FCSTD DOCUMENT  (FreeCAD 1.0RUnknown)
Label: wardrobe_drawer_jan
License: All rights reserved
objects: App::FeaturePython×11, App::Link×7, Assembly::JointGroup×1, Assembly::AssemblyObject×1
EXTERNAL_REF file=../purchased parts/hettich_rail_550mm.FCStd obj=Body
EXTERNAL_REF file=parts/drawer_sides.FCStd obj=Body
EXTERNAL_REF file=parts/drawer_back.FCStd obj=Body
EXTERNAL_REF file=parts/drawer_bottom.FCStd obj=Body
EXTERNAL_REF file=parts/drawer_front.FCStd obj=Body

FEATURE [App::Link] hettich_rail_550
  LinkPlacement = pos=(0,-8.67788e-07,0) rot=(0.57735,0.57735,0.57735;2.0944rad)
  LinkedObject = -> <external ../purchased parts/hettich_rail_550mm.FCStd>#Body
  Placement = pos=(0,-8.67788e-07,0) rot=(0.57735,0.57735,0.57735;2.0944rad)
FEATURE [App::Link] hettich_rail_551  label="hettich_rail_550_1"
  LinkPlacement = pos=(502,3.32992e-05,-3.4167e-05) rot=(0.57735,-0.57735,-0.57735;2.0944rad)
  LinkedObject = -> <external ../purchased parts/hettich_rail_550mm.FCStd>#Body
  Placement = pos=(502,3.32992e-05,-3.4167e-05) rot=(0.57735,-0.57735,-0.57735;2.0944rad)
FEATURE [App::Link] drawer_sides
  LinkPlacement = pos=(22,256,72.5) rot=(-0.340731,0.659269,0.659269;0rad)
  LinkedObject = -> <external parts/drawer_sides.FCStd>#Body
  Placement = pos=(22,256,72.5) rot=(-0.340731,0.659269,0.659269;0rad)
FEATURE [App::Link] drawer_sides001
  LinkPlacement = pos=(480,-256,72.5) rot=(0,0,1;3.14159rad)
  LinkedObject = -> <external parts/drawer_sides.FCStd>#Body
  Placement = pos=(480,-256,72.5) rot=(0,0,1;3.14159rad)
FEATURE [App::Link] drawer_back
  LinkPlacement = pos=(489.5,265.5,80.75) rot=(0,0,-1;1.5708rad)
  LinkedObject = -> <external parts/drawer_back.FCStd>#Body
  Placement = pos=(489.5,265.5,80.75) rot=(0,0,-1;1.5708rad)
FEATURE [App::Link] drawer_bottom
  LinkPlacement = pos=(251,5.75002,-2.50002) rot=(0,0,1;3.14159rad)
  LinkedObject = -> <external parts/drawer_bottom.FCStd>#Body
  Placement = pos=(251,5.75002,-2.50002) rot=(0,0,1;3.14159rad)
FEATURE [App::Link] drawer_front
  LinkPlacement = pos=(12.5,-265.5,72.5) rot=(0,0,1;1.5708rad)
  LinkedObject = -> <external parts/drawer_front.FCStd>#Body
  Placement = pos=(12.5,-265.5,72.5) rot=(0,0,1;1.5708rad)
FEATURE [App::FeaturePython] GroundedJoint  # Assembly grounded joint (typed FeaturePython)
  ObjectToGround = -> hettich_rail_550
  Placement = pos=(0,-8.67788e-07,0) rot=(0.57735,0.57735,0.57735;2.0944rad)
FEATURE [App::FeaturePython] Joint  label="Gleitverbindung"  # Assembly joint (typed FeaturePython)
  Activated = true
  AngleMax = 0
  AngleMin = 0
  Detach1 = false
  Detach2 = false
  Distance = 0
  Distance2 = 0
  EnableAngleMax = false
  EnableAngleMin = false
  EnableLengthMax = true
  EnableLengthMin = true
  JointType = 3 (Slider)
  LengthMax = 275
  LengthMin = -100
  Offset2 = pos=(0,0,0) rot=(0,0,1;1.5708rad)
  Placement1 = pos=(-9.5,-256,-85) rot=(-0.57735,-0.57735,0.57735;4.18879rad)
  Placement2 = pos=(-275,-12.5,12.5) rot=(-0.57735,0.57735,0.57735;4.18879rad)
  Reference1 = -> Assembly [drawer_sides.Edge8,drawer_sides.Edge8]
  Reference2 = -> Assembly [hettich_rail_550.Edge16,hettich_rail_550.Vertex11]
FEATURE [App::FeaturePython] Joint003  label="Parallel"  # Assembly joint (typed FeaturePython)
  Activated = true
  AngleMax = 0
  AngleMin = 0
  Detach1 = false
  Detach2 = false
  Distance = 0
  Distance2 = 0
  EnableAngleMax = false
  EnableAngleMin = false
  EnableLengthMax = false
  EnableLengthMin = false
  JointType = 6 (Parallel)
  LengthMax = 0
  LengthMin = 0
  Placement1 = pos=(275,-12.5,12.5) rot=(0,0,1;0rad)
  Placement2 = pos=(-4e-16,2.5,12.5) rot=(0,0,1;0rad)
  Reference1 = -> Assembly [hettich_rail_550.Face5,hettich_rail_550.Vertex12]
  Reference2 = -> Assembly [hettich_rail_551.Face5,hettich_rail_551.Face5]
FEATURE [App::FeaturePython] Joint004  label="Parallel001"  # Assembly joint (typed FeaturePython)
  Activated = true
  AngleMax = 0
  AngleMin = 0
  Detach1 = false
  Detach2 = false
  Distance = 0
  Distance2 = 0
  EnableAngleMax = false
  EnableAngleMin = false
  EnableLengthMax = false
  EnableLengthMin = false
  JointType = 6 (Parallel)
  LengthMax = 0
  LengthMin = 0
  Placement1 = pos=(275,-12.5,25.5) rot=(0,-0.707107,0.707107;3.14159rad)
  Placement2 = pos=(-275,-12.5,25.5) rot=(0,0.707107,-0.707107;3.14159rad)
  Reference1 = -> Assembly [hettich_rail_550.Face7,hettich_rail_550.Vertex15]
  Reference2 = -> Assembly [hettich_rail_551.Face7,hettich_rail_551.Vertex16]
FEATURE [App::FeaturePython] Joint005  label="Parallel002"  # Assembly joint (typed FeaturePython)
  Activated = true
  AngleMax = 0
  AngleMin = 0
  Detach1 = false
  Detach2 = false
  Distance = 0
  Distance2 = 0
  EnableAngleMax = false
  EnableAngleMin = false
  EnableLengthMax = false
  EnableLengthMin = false
  JointType = 6 (Parallel)
  LengthMax = 0
  LengthMin = 0
  Placement1 = pos=(275,-0.565372,6.79404) rot=(-0.707107,0,-0.707107;3.14159rad)
  Placement2 = pos=(-275,-0.565372,6.79404) rot=(-0.707107,0,0.707107;3.14159rad)
  Reference1 = -> Assembly [hettich_rail_550.Face10,hettich_rail_550.Face10]
  Reference2 = -> Assembly [hettich_rail_551.Face9,hettich_rail_551.Face9]
FEATURE [App::FeaturePython] Joint006  label="Abstand"  # Assembly joint (typed FeaturePython)
  Activated = true
  AngleMax = 0
  AngleMin = 0
  Detach1 = false
  Detach2 = false
  Distance = 0
  Distance2 = 0
  EnableAngleMax = false
  EnableAngleMin = false
  EnableLengthMax = false
  EnableLengthMin = false
  JointType = 5 (Distance)
  LengthMax = 0
  LengthMin = 0
  Placement1 = pos=(275,-0.565372,6.79404) rot=(-0.707107,0,-0.707107;3.14159rad)
  Placement2 = pos=(-275,-0.565372,6.79404) rot=(-0.707107,0,0.707107;3.14159rad)
  Reference1 = -> Assembly [hettich_rail_550.Face10,hettich_rail_550.Face10]
  Reference2 = -> Assembly [hettich_rail_551.Face9,hettich_rail_551.Face9]
FEATURE [App::FeaturePython] Joint007  label="StarrerVerbund"  # Assembly joint (typed FeaturePython)
  Activated = true
  AngleMax = 0
  AngleMin = 0
  Detach1 = false
  Detach2 = false
  Distance = 0
  Distance2 = 0
  EnableAngleMax = false
  EnableAngleMin = false
  EnableLengthMax = false
  EnableLengthMin = false
  JointType = 0 (Fixed)
  LengthMax = 0
  LengthMin = 0
  Offset2 = pos=(0,0,0) rot=(0,0,1;1.5708rad)
  Placement1 = pos=(9.5,1.8e-15,85) rot=(0,0,1;0rad)
  Placement2 = pos=(-9.5,-512,85) rot=(0.707107,0.707107,0;3.14159rad)
  Reference1 = -> Assembly [drawer_front.Edge3,drawer_front.Vertex3]
  Reference2 = -> Assembly [drawer_sides.Edge10,drawer_sides.Vertex6]
FEATURE [App::FeaturePython] Joint009  label="Gleitverbindung001"  # Assembly joint (typed FeaturePython)
  Activated = true
  AngleMax = 0
  AngleMin = 0
  Detach1 = false
  Detach2 = false
  Distance = 0
  Distance2 = 0
  EnableAngleMax = false
  EnableAngleMin = false
  EnableLengthMax = false
  EnableLengthMin = false
  JointType = 3 (Slider)
  LengthMax = 0
  LengthMin = 0
  Placement1 = pos=(275,-12.5,12.5) rot=(-0.707107,0,0.707107;3.14159rad)
  Placement2 = pos=(-9.5,-256,-85) rot=(-0.57735,-0.57735,0.57735;4.18879rad)
  Reference1 = -> Assembly [hettich_rail_551.Edge16,hettich_rail_551.Vertex12]
  Reference2 = -> Assembly [drawer_sides001.Edge8,drawer_sides001.Edge8]
FEATURE [App::FeaturePython] Joint010  label="StarrerVerbund002"  # Assembly joint (typed FeaturePython)
  Activated = true
  AngleMax = 0
  AngleMin = 0
  Detach1 = false
  Detach2 = false
  Distance = 0
  Distance2 = 0
  EnableAngleMax = false
  EnableAngleMin = false
  EnableLengthMax = false
  EnableLengthMin = false
  JointType = 0 (Fixed)
  LengthMax = 0
  LengthMin = 0
  Offset2 = pos=(0,0,0) rot=(0,0,-1;1.5708rad)
  Placement1 = pos=(9.5,-477,76.75) rot=(0,0,1;0rad)
  Placement2 = pos=(-9.5,-5.68e-14,85) rot=(-0.707107,0.707107,0;3.14159rad)
  Reference1 = -> Assembly [drawer_back.Edge7,drawer_back.Vertex6]
  Reference2 = -> Assembly [drawer_sides.Edge9,drawer_sides.Vertex5]
FEATURE [App::FeaturePython] Joint011  label="StarrerVerbund003"  # Assembly joint (typed FeaturePython)
  Activated = true
  AngleMax = 0
  AngleMin = 0
  Detach1 = false
  Detach2 = false
  Distance = 0
  Distance2 = 0
  EnableAngleMax = false
  EnableAngleMin = false
  EnableLengthMax = false
  EnableLengthMin = false
  JointType = 0 (Fixed)
  LengthMax = 0
  LengthMin = 0
  Placement1 = pos=(-9.5,0,85) rot=(0,1,0;3.14159rad)
  Placement2 = pos=(9.5,-477,85) rot=(0,0,1;0rad)
  Reference1 = -> Assembly [drawer_sides001.Edge9,drawer_sides001.Vertex5]
  Reference2 = -> Assembly [drawer_front.Edge4,drawer_front.Vertex4]
FEATURE [App::FeaturePython] Joint012  label="StarrerVerbund004"  # Assembly joint (typed FeaturePython)
  Activated = true
  AngleMax = 0
  AngleMin = 0
  Detach1 = false
  Detach2 = false
  Distance = 0
  Distance2 = 0
  EnableAngleMax = false
  EnableAngleMin = false
  EnableLengthMax = false
  EnableLengthMin = false
  JointType = 0 (Fixed)
  LengthMax = 0
  LengthMin = 0
  Placement1 = pos=(0,269.75,0) rot=(-0.707107,0,0.707107;3.14159rad)
  Placement2 = pos=(1.5,-238.5,-75) rot=(-0.57735,-0.57735,0.57735;4.18879rad)
  Reference1 = -> Assembly [drawer_bottom.Edge9,drawer_bottom.Edge9]
  Reference2 = -> Assembly [drawer_front.Edge17,drawer_front.Edge17]
FEATURE [Assembly::JointGroup] Joints
  Group = -> [GroundedJoint,Joint,Joint003,Joint004,Joint005,Joint006,Joint007,Joint009,Joint010,Joint011,Joint012]
FEATURE [Assembly::AssemblyObject] Assembly  label="wardrobe_drawer_jan"
  Group = -> [Joints,hettich_rail_550,hettich_rail_551,drawer_sides,drawer_sides001,drawer_back,drawer_bottom,drawer_front,GroundedJoint,Joint,Joint003,Joint004,Joint005,Joint006,Joint007,Joint009,Joint010,Joint011,Joint012]
  Origin = -> Origin
  Type = Assembly

RESOLVED EXTERNAL PARTS (link-assembly join: the EXTERNAL_REF files above that resolve inside this repo's crawl, each included once):
---- part parts/drawer_back.FCStd = doc fcstd_10e94b67beff ----
FCSTD DOCUMENT  (FreeCAD 1.0RUnknown)
Label: drawer_back
License: All rights reserved
objects: PartDesign::CoordinateSystem×2, Sketcher::SketchObject×1, PartDesign::Pad×1, PartDesign::Body×1
note: 8 computed .brp shape members not serialized (recipe doc carries the construction recipe); baked Part::Feature solids carry a one-line shape summary decoded from their .brp
EXTERNAL_REF file=../../mastersketch.FCStd obj=Spreadsheet

FEATURE [Sketcher::SketchObject] Sketch
  ArcFitTolerance = 1e-06
  AttachmentSupport = -> [XZ_Plane]
  FullyConstrained = true
  MakeInternals = false
  MapMode = 5
  Placement = pos=(0,0,0) rot=(1,0,0;1.5708rad)
  expr: Constraints[10] = mastersketch#Spreadsheet.drawer_outer_thickness
  expr: Constraints[11] = mastersketch#Spreadsheet.drawer_height - (mastersketch#Spreadsheet.drawer_bottom_thickness + mastersketch#Spreadsheet.drawer_bottom_tol + mastersketch#Spreadsheet.drawer_slot_height)
  sketch-geometry (5):
    g0: LineSegment StartX=-9.5 StartY=-76.75 StartZ=0 EndX=9.5 EndY=-76.75 EndZ=0
    g1: LineSegment StartX=9.5 StartY=-76.75 StartZ=0 EndX=9.5 EndY=76.75 EndZ=0
    g2: LineSegment StartX=9.5 StartY=76.75 StartZ=0 EndX=-9.5 EndY=76.75 EndZ=0
    g3: LineSegment StartX=-9.5 StartY=76.75 StartZ=0 EndX=-9.5 EndY=-76.75 EndZ=0
    g4: GeomPoint [constr] X=0 Y=0 Z=0
  constraints (12):
    c: Coincident(g0,g1)
    c: Coincident(g1,g2)
    c: Coincident(g2,g3)
    c: Coincident(g3,g0)
    c: Horizontal(g0)
    c: Horizontal(g2)
    c: Vertical(g1)
    c: Vertical(g3)
    c: Symmetric(g2,g0,g4)
    c: Coincident(g4,g-1)
    c: DistanceX(g0,g0) = 19
    c: DistanceY(g1,g1) = 153.5
FEATURE [PartDesign::Pad] Pad
  Direction = (0,-1,2e-16)
  Length = 477
  Length2 = 10
  Placement = pos=(0,0,0) rot=(1,0,0;1.5708rad)
  Profile = -> Sketch
  ReferenceAxis = -> Sketch [N_Axis]
  Refine = true
  Suppressed = false
  Type = 0
  expr: Length = mastersketch#Spreadsheet.drawer_width
FEATURE [PartDesign::CoordinateSystem] LCS_left
  AttacherType = Attacher::AttachEngine3D
  AttachmentSupport = -> [Pad]
  MapMode = 7
  Placement = pos=(9.5,-477,76.75) rot=(0,1,0;3.14159rad)
FEATURE [PartDesign::CoordinateSystem] LCS_right
  AttacherType = Attacher::AttachEngine3D
  AttachmentSupport = -> [Pad]
  MapMode = 7
  Placement = pos=(9.5,0,76.75) rot=(0,1,0;3.14159rad)
FEATURE [PartDesign::Body] Body  label="drawer_back"
  AllowCompound = false
  Group = -> [Sketch,Pad,LCS_left,LCS_right]
  Origin = -> Origin
  Tip = -> Pad
---- part parts/drawer_bottom.FCStd = doc fcstd_674dae41beb6 ----
FCSTD DOCUMENT  (FreeCAD 1.0RUnknown)
Label: drawer_bottom
License: All rights reserved
objects: Sketcher::SketchObject×1, PartDesign::Pad×1, PartDesign::CoordinateSystem×1, PartDesign::Body×1
note: 7 computed .brp shape members not serialized (recipe doc carries the construction recipe); baked Part::Feature solids carry a one-line shape summary decoded from their .brp
EXTERNAL_REF file=../../mastersketch.FCStd obj=Spreadsheet

FEATURE [Sketcher::SketchObject] Sketch
  ArcFitTolerance = 1e-06
  AttachmentSupport = -> [XY_Plane]
  FullyConstrained = true
  MakeInternals = false
  MapMode = 5
  expr: Constraints[10] = mastersketch#Spreadsheet.drawer_width + 2 * (mastersketch#Spreadsheet.drawer_slot_depth + mastersketch#Spreadsheet.drawer_bottom_tol) - 2 * mastersketch#Spreadsheet.drawer_outer_thickness - 2
  expr: Constraints[11] = mastersketch#Spreadsheet.drawer_length + mastersketch#Spreadsheet.drawer_slot_depth + mastersketch#Spreadsheet.drawer_bottom_tol - mastersketch#Spreadsheet.drawer_outer_thickness
  sketch-geometry (5):
    g0: LineSegment StartX=-227 StartY=-269.75 StartZ=0 EndX=227 EndY=-269.75 EndZ=0
    g1: LineSegment StartX=227 StartY=-269.75 StartZ=0 EndX=227 EndY=269.75 EndZ=0
    g2: LineSegment StartX=227 StartY=269.75 StartZ=0 EndX=-227 EndY=269.75 EndZ=0
    g3: LineSegment StartX=-227 StartY=269.75 StartZ=0 EndX=-227 EndY=-269.75 EndZ=0
    g4: GeomPoint [constr] X=0 Y=0 Z=0
  constraints (12):
    c: Coincident(g0,g1)
    c: Coincident(g1,g2)
    c: Coincident(g2,g3)
    c: Coincident(g3,g0)
    c: Horizontal(g0)
    c: Horizontal(g2)
    c: Vertical(g1)
    c: Vertical(g3)
    c: Symmetric(g2,g0,g4)
    c: Coincident(g4,g-1)
    c: DistanceX(g0,g0) = 454
    c: DistanceY(g1,g1) = 539.5
FEATURE [PartDesign::Pad] Pad
  Direction = (0,0,1)
  Length = 6
  Length2 = 10
  Profile = -> Sketch
  ReferenceAxis = -> Sketch [N_Axis]
  Refine = true
  Suppressed = false
  Type = 0
  expr: Length = mastersketch#Spreadsheet.drawer_bottom_thickness
FEATURE [PartDesign::CoordinateSystem] LCS_front
  AttacherType = Attacher::AttachEngine3D
  AttachmentSupport = -> [Pad]
  MapMode = 45
  Placement = pos=(0,-269.75,0) rot=(0.57735,0.57735,0.57735;2.0944rad)
FEATURE [PartDesign::Body] Body  label="drawer_bottom"
  AllowCompound = false
  Group = -> [Sketch,Pad,LCS_front]
  Origin = -> Origin
  Tip = -> Pad
---- part parts/drawer_front.FCStd = doc fcstd_8f72376a405c ----
FCSTD DOCUMENT  (FreeCAD 1.0RUnknown)
Label: drawer_front
License: All rights reserved
objects: PartDesign::CoordinateSystem×3, Sketcher::SketchObject×1, PartDesign::Pad×1, PartDesign::Body×1
note: 9 computed .brp shape members not serialized (recipe doc carries the construction recipe); baked Part::Feature solids carry a one-line shape summary decoded from their .brp
EXTERNAL_REF file=../../mastersketch.FCStd obj=Spreadsheet

FEATURE [Sketcher::SketchObject] Sketch
  ArcFitTolerance = 1e-06
  AttachmentSupport = -> [XZ_Plane]
  FullyConstrained = true
  MakeInternals = false
  MapMode = 5
  Placement = pos=(0,0,0) rot=(1,0,0;1.5708rad)
  expr: Constraints[13] = mastersketch#Spreadsheet.drawer_outer_thickness
  expr: Constraints[19] = mastersketch#Spreadsheet.drawer_bottom_thickness + mastersketch#Spreadsheet.drawer_bottom_tol
  expr: Constraints[20] = mastersketch#Spreadsheet.drawer_slot_height
  expr: Constraints[21] = mastersketch#Spreadsheet.drawer_height
  expr: Constraints[22] = mastersketch#Spreadsheet.drawer_slot_depth
  sketch-geometry (9):
    g0: LineSegment StartX=-9.5 StartY=-85 StartZ=0 EndX=9.5 EndY=-85 EndZ=0
    g1: LineSegment StartX=9.5 StartY=-85 StartZ=0 EndX=9.5 EndY=-75 EndZ=0
    g2: LineSegment StartX=9.5 StartY=85 StartZ=0 EndX=-9.5 EndY=85 EndZ=0
    g3: LineSegment StartX=-9.5 StartY=85 StartZ=0 EndX=-9.5 EndY=-85 EndZ=0
    g4: GeomPoint [constr] X=0 Y=0 Z=0
    g5: LineSegment StartX=9.5 StartY=-68.5 StartZ=0 EndX=1.5 EndY=-68.5 EndZ=0
    g6: LineSegment StartX=1.5 StartY=-68.5 StartZ=0 EndX=1.5 EndY=-75 EndZ=0
    g7: LineSegment StartX=1.5 StartY=-75 StartZ=0 EndX=9.5 EndY=-75 EndZ=0
    g8: LineSegment StartX=9.5 StartY=-68.5 StartZ=0 EndX=9.5 EndY=85 EndZ=0
  constraints (23):
    c: Coincident(g0,g1)
    c: Coincident(g8,g2)
    c: Coincident(g2,g3)
    c: Coincident(g3,g0)
    c: Horizontal(g0)
    c: Vertical(g1)
    c: Symmetric(g2,g0,g4)
    c: Coincident(g4,g-1)
    c: Coincident(g5,g6)
    c: Coincident(g6,g7)
    c: Vertical(g6)
    c: Horizontal(g5)
    c: Horizontal(g7)
    c: DistanceX(g2,g2) = 19
    c: Parallel(g3,g8)
    c: Coincident(g5,g8)
    c: Coincident(g7,g1)
    c: Vertical(g5,g1)
    c: Symmetric(g2,g2,g-2)
    c: Distance(g5,g1) = 6.5
    c: Distance(g6,g0) = 10
    c: DistanceY(g3,g3) = 170
    c: DistanceX(g5,g5) = 8
FEATURE [PartDesign::Pad] Pad
  Direction = (0,-1,2e-16)
  Length = 477
  Length2 = 10
  Placement = pos=(0,0,0) rot=(1,0,0;1.5708rad)
  Profile = -> Sketch
  ReferenceAxis = -> Sketch [N_Axis]
  Refine = true
  Suppressed = false
  Type = 0
  expr: Length = mastersketch#Spreadsheet.drawer_width
FEATURE [PartDesign::CoordinateSystem] LCS_left
  AttacherType = Attacher::AttachEngine3D
  AttachmentSupport = -> [Pad]
  MapMode = 7
  Placement = pos=(9.5,0,85) rot=(0,1,0;3.14159rad)
FEATURE [PartDesign::CoordinateSystem] LCS_right
  AttacherType = Attacher::AttachEngine3D
  AttachmentSupport = -> [Pad]
  MapMode = 7
  Placement = pos=(9.5,-477,85) rot=(0,1,0;3.14159rad)
FEATURE [PartDesign::CoordinateSystem] LCS_bottom_center
  AttacherType = Attacher::AttachEngine3D
  AttachmentSupport = -> [Pad]
  MapMode = 45
  Placement = pos=(1.5,-238.5,-75) rot=(0,0.707107,0.707107;3.14159rad)
FEATURE [PartDesign::Body] Body  label="drawer_front"
  AllowCompound = false
  Group = -> [Sketch,Pad,LCS_left,LCS_right,LCS_bottom_center]
  Origin = -> Origin
  Tip = -> Pad
---- part parts/drawer_sides.FCStd = doc fcstd_b4c7660c6d1a ----
FCSTD DOCUMENT  (FreeCAD 1.0RUnknown)
Label: drawer_sides
License: All rights reserved
objects: PartDesign::CoordinateSystem×3, Sketcher::SketchObject×1, PartDesign::Pad×1, PartDesign::Body×1
note: 9 computed .brp shape members not serialized (recipe doc carries the construction recipe); baked Part::Feature solids carry a one-line shape summary decoded from their .brp
EXTERNAL_REF file=../../mastersketch.FCStd obj=Spreadsheet

FEATURE [Sketcher::SketchObject] Sketch
  ArcFitTolerance = 1e-06
  AttachmentSupport = -> [XZ_Plane]
  FullyConstrained = true
  MakeInternals = false
  MapMode = 5
  Placement = pos=(0,0,0) rot=(1,0,0;1.5708rad)
  expr: Constraints[13] = mastersketch#Spreadsheet.drawer_outer_thickness
  expr: Constraints[19] = mastersketch#Spreadsheet.drawer_bottom_thickness + mastersketch#Spreadsheet.drawer_bottom_tol
  expr: Constraints[20] = mastersketch#Spreadsheet.drawer_slot_height
  expr: Constraints[21] = mastersketch#Spreadsheet.drawer_height
  expr: Constraints[22] = mastersketch#Spreadsheet.drawer_slot_depth
  sketch-geometry (9):
    g0: LineSegment StartX=-9.5 StartY=-85 StartZ=0 EndX=9.5 EndY=-85 EndZ=0
    g1: LineSegment StartX=9.5 StartY=-85 StartZ=0 EndX=9.5 EndY=-75 EndZ=0
    g2: LineSegment StartX=9.5 StartY=85 StartZ=0 EndX=-9.5 EndY=85 EndZ=0
    g3: LineSegment StartX=-9.5 StartY=85 StartZ=0 EndX=-9.5 EndY=-85 EndZ=0
    g4: GeomPoint [constr] X=0 Y=0 Z=0
    g5: LineSegment StartX=9.5 StartY=-68.5 StartZ=0 EndX=1.5 EndY=-68.5 EndZ=0
    g6: LineSegment StartX=1.5 StartY=-68.5 StartZ=0 EndX=1.5 EndY=-75 EndZ=0
    g7: LineSegment StartX=1.5 StartY=-75 StartZ=0 EndX=9.5 EndY=-75 EndZ=0
    g8: LineSegment StartX=9.5 StartY=-68.5 StartZ=0 EndX=9.5 EndY=85 EndZ=0
  constraints (23):
    c: Coincident(g0,g1)
    c: Coincident(g8,g2)
    c: Coincident(g2,g3)
    c: Coincident(g3,g0)
    c: Horizontal(g0)
    c: Vertical(g1)
    c: Symmetric(g2,g0,g4)
    c: Coincident(g4,g-1)
    c: Coincident(g5,g6)
    c: Coincident(g6,g7)
    c: Vertical(g6)
    c: Horizontal(g5)
    c: Horizontal(g7)
    c: DistanceX(g2,g2) = 19
    c: Parallel(g3,g8)
    c: Coincident(g5,g8)
    c: Coincident(g7,g1)
    c: Vertical(g5,g1)
    c: Symmetric(g2,g2,g-2)
    c: Distance(g5,g1) = 6.5
    c: Distance(g6,g0) = 10
    c: DistanceY(g3,g3) = 170
    c: DistanceX(g5,g5) = 8
FEATURE [PartDesign::Pad] Pad
  Direction = (0,-1,2e-16)
  Length = 512
  Length2 = 10
  Placement = pos=(0,0,0) rot=(1,0,0;1.5708rad)
  Profile = -> Sketch
  ReferenceAxis = -> Sketch [N_Axis]
  Refine = true
  Suppressed = false
  Type = 0
  expr: Length = mastersketch#Spreadsheet.drawer_length - 2 * mastersketch#Spreadsheet.drawer_outer_thickness
FEATURE [PartDesign::CoordinateSystem] LCS_bottom_center
  AttacherType = Attacher::AttachEngine3D
  AttachmentSupport = -> [Pad]
  MapMode = 45
  Placement = pos=(-9.5,-256,-85) rot=(0,0.707107,0.707107;3.14159rad)
FEATURE [PartDesign::CoordinateSystem] LCS_1
  AttacherType = Attacher::AttachEngine3D
  AttachmentSupport = -> [Pad]
  MapMode = 7
  Placement = pos=(-9.5,-512,85) rot=(0,0,1;0rad)
FEATURE [PartDesign::CoordinateSystem] LCS_2
  AttacherType = Attacher::AttachEngine3D
  AttachmentSupport = -> [Pad]
  MapMode = 7
  Placement = pos=(-9.5,0,85) rot=(0,0,1;0rad)
FEATURE [PartDesign::Body] Body  label="drawer_sides"
  AllowCompound = false
  Group = -> [Sketch,Pad,LCS_bottom_center,LCS_1,LCS_2]
  Origin = -> Origin
  Tip = -> Pad
